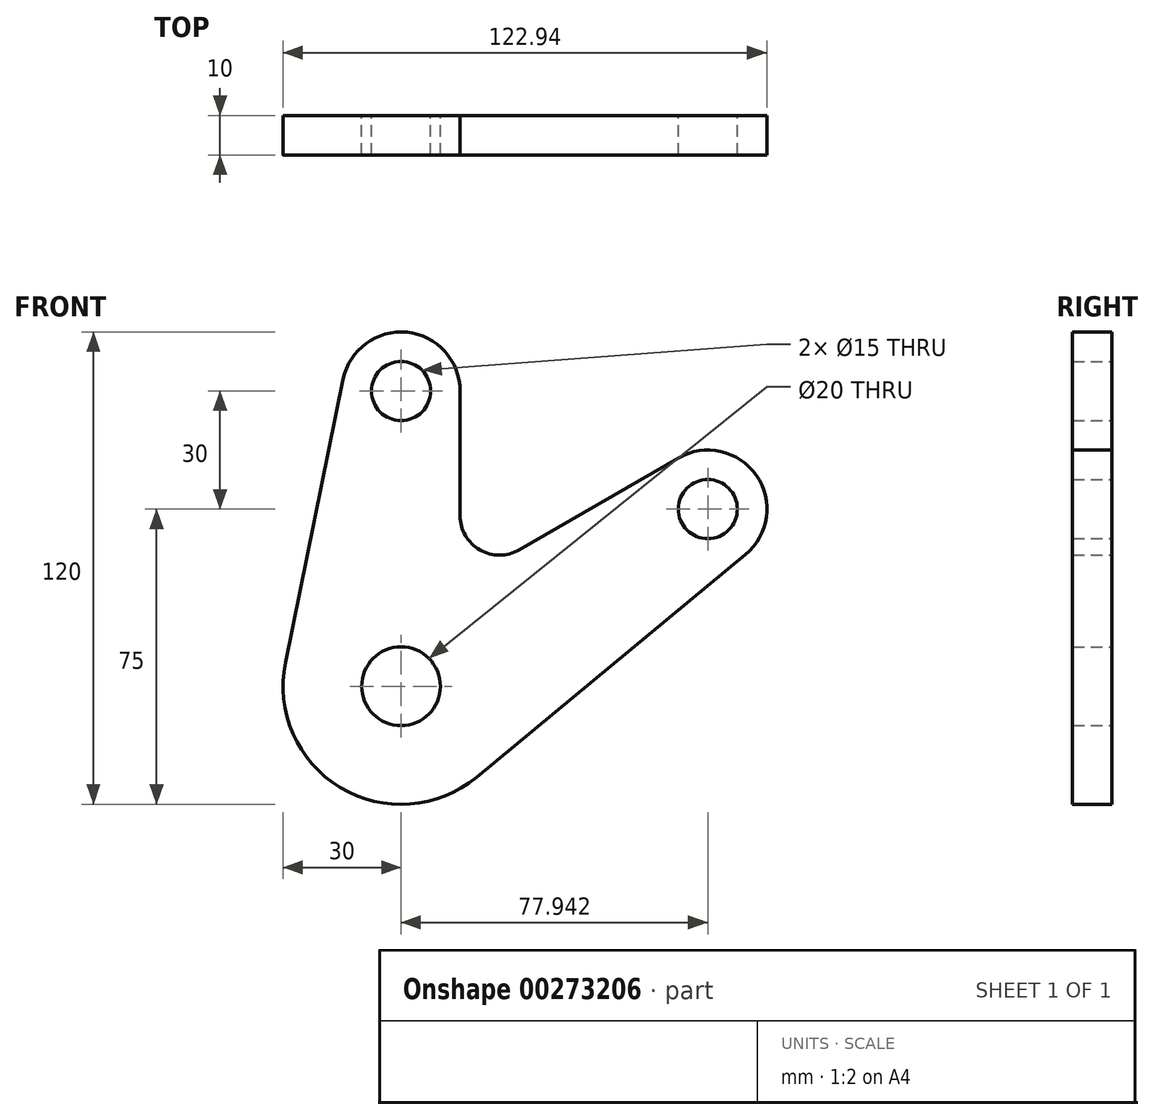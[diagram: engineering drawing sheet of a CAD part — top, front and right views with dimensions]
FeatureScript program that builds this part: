
annotation { "Feature Type Name" : "Feature", "Feature Type Description" : "" }
export const myFeature = defineFeature(function(context is Context, id is Id, definition is map)
    precondition{}
    {
        {
            var Q0;
            Q0=qCreatedBy(makeId("Front.planeOp"),FACE);
            var sketch = newSketch(context, id + "F0", { "sketchPlane" : qUnion([Q0])});
            skLineSegment(sketch, "E0", {"start": v(0, 0) * mm, "end": v(0, 75) * mm, "construction": true});
            skLineSegment(sketch, "E1", {"start": v(0, 0) * mm, "end": v(77.94, 45) * mm, "construction": true});
            skCircle(sketch, "E2", {"center": v(0, 0) * mm, "radius": 10 * mm});
            skCircle(sketch, "E3", {"center": v(77.94, 45) * mm, "radius": 7.5 * mm});
            skCircle(sketch, "E4", {"center": v(0, 75) * mm, "radius": 7.5 * mm});
            skArc(sketch, "E5", {"start": v(-14.7, 78) * mm, "mid": v(1.5, 89.92) * mm, "end": v(15, 75) * mm});
            skArc(sketch, "E6", {"start": v(70.44, 58) * mm, "mid": v(90.26, 53.56) * mm, "end": v(87.5, 33.44) * mm});
            skArc(sketch, "E7", {"start": v(-29.4, 6) * mm, "mid": v(-15.44, -25.72) * mm, "end": v(19.12, -23.12) * mm});
            skLineSegment(sketch, "E8", {"start": v(-29.4, 6) * mm, "end": v(-14.7, 78) * mm});
            skLineSegment(sketch, "E9", {"start": v(19.12, -23.12) * mm, "end": v(87.5, 33.44) * mm});
            skLineSegment(sketch, "E10", {"start": v(15, 75) * mm, "end": v(15, 43.3) * mm});
            skArc(sketch, "E11", {"start": v(15, 43.3) * mm, "mid": v(20, 34.64) * mm, "end": v(30, 34.64) * mm});
            skLineSegment(sketch, "E12", {"start": v(30, 34.64) * mm, "end": v(70.44, 58) * mm});
            skSolve(sketch);
        }
        {
            var Q0;
            Q0=makeQuery(id+"F0.imprint","IMPRINT",FACE,{"disambiguationData":[TD([[makeQuery(id+"F0.imprint","IMPRINT",EDGE,{"derivedFrom":sQuery(id+"F0.wireOp",EDGE,"E2")}),-1.0]])]});
            extrude(context, id + "F1", {"entities" : qUnion([Q0]), "depth" : 10 * mm});
        }
    });
